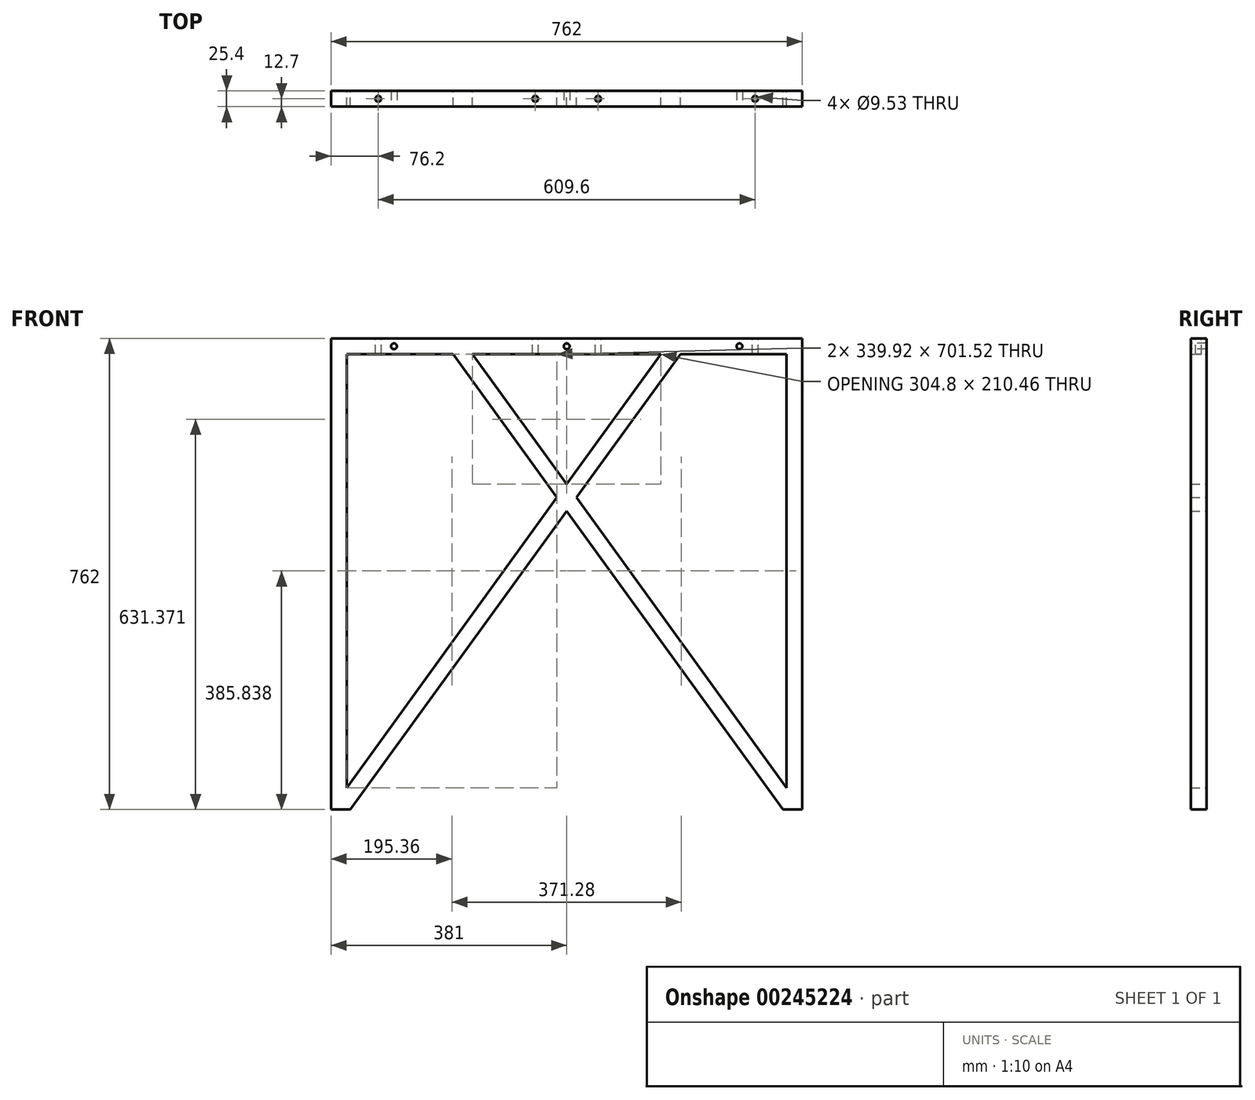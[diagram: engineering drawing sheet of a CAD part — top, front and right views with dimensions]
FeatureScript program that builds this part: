
annotation { "Feature Type Name" : "Feature", "Feature Type Description" : "" }
export const myFeature = defineFeature(function(context is Context, id is Id, definition is map)
    precondition{}
    {
        {
            var Q0;
            Q0=qCreatedBy(makeId("Front.planeOp"),FACE);
            var sketch = newSketch(context, id + "F0", { "sketchPlane" : qUnion([Q0])});
            skLineSegment(sketch, "E0.bottom", {"start": v(-381, 762) * mm, "end": v(381, 762) * mm});
            skLineSegment(sketch, "E0.left", {"start": v(-381, 762) * mm, "end": v(-381, 0) * mm});
            skLineSegment(sketch, "E0.right", {"start": v(381, 762) * mm, "end": v(381, 0) * mm});
            skLineSegment(sketch, "E1", {"start": v(0, 762) * mm, "end": v(0, 0) * mm, "construction": true});
            skLineSegment(sketch, "E2.0", {"start": v(-355.6, 736.6) * mm, "end": v(-355.6, 35.08) * mm});
            skLineSegment(sketch, "E2.2", {"start": v(355.6, 736.6) * mm, "end": v(355.6, 35.08) * mm});
            skLineSegment(sketch, "E3", {"start": v(-355.6, 35.08) * mm, "end": v(-15.68, 504.49) * mm});
            skLineSegment(sketch, "E4.0", {"start": v(-349.64, 0) * mm, "end": v(0, 482.84) * mm});
            skLineSegment(sketch, "E5", {"start": v(-381, 0) * mm, "end": v(-349.64, 0) * mm});
            skLineSegment(sketch, "E6.MirrorCS", {"start": v(349.64, 0) * mm, "end": v(0, 482.84) * mm});
            skLineSegment(sketch, "E7.MirrorCS", {"start": v(355.6, 35.08) * mm, "end": v(15.68, 504.49) * mm});
            skLineSegment(sketch, "E8", {"start": v(381, 0) * mm, "end": v(349.64, 0) * mm});
            skLineSegment(sketch, "E9", {"start": v(-355.6, 736.6) * mm, "end": v(-183.76, 736.6) * mm});
            skLineSegment(sketch, "E10.trimOffspring", {"start": v(-152.4, 736.6) * mm, "end": v(152.4, 736.6) * mm});
            skLineSegment(sketch, "E11.trimOffspring", {"start": v(183.76, 736.6) * mm, "end": v(355.6, 736.6) * mm});
            skLineSegment(sketch, "E12.trimOffspring", {"start": v(15.68, 504.49) * mm, "end": v(183.76, 736.6) * mm});
            skLineSegment(sketch, "E13.trimOffspring", {"start": v(0, 526.14) * mm, "end": v(152.4, 736.6) * mm});
            skLineSegment(sketch, "E14.trimOffspring", {"start": v(0, 526.14) * mm, "end": v(-152.4, 736.6) * mm});
            skLineSegment(sketch, "E15.trimOffspring", {"start": v(-15.68, 504.49) * mm, "end": v(-183.76, 736.6) * mm});
            skSolve(sketch);
        }
        {
            var Q0;
            Q0 = qSketchRegion(id + "F0", true);
            extrude(context, id + "F1", {"entities" : qUnion([Q0]), "depth" : 25.4 * mm});
        }
        {
            var Q0;
            Q0=makeQuery(id+"F1.opExtrude","CAP_FACE",FACE,{"disambiguationData":[OSD([sQuery(id+"F0.wireOp",EDGE,"E0.bottom"),sQuery(id+"F0.wireOp",EDGE,"E0.left"),sQuery(id+"F0.wireOp",EDGE,"E0.right"),sQuery(id+"F0.wireOp",EDGE,"E2.0"),sQuery(id+"F0.wireOp",EDGE,"E2.2"),sQuery(id+"F0.wireOp",EDGE,"E3"),sQuery(id+"F0.wireOp",EDGE,"E4.0"),sQuery(id+"F0.wireOp",EDGE,"E5"),sQuery(id+"F0.wireOp",EDGE,"E6.MirrorCS"),sQuery(id+"F0.wireOp",EDGE,"E7.MirrorCS"),sQuery(id+"F0.wireOp",EDGE,"E8"),sQuery(id+"F0.wireOp",EDGE,"E9"),sQuery(id+"F0.wireOp",EDGE,"E10.trimOffspring"),sQuery(id+"F0.wireOp",EDGE,"E11.trimOffspring"),sQuery(id+"F0.wireOp",EDGE,"E12.trimOffspring"),sQuery(id+"F0.wireOp",EDGE,"E13.trimOffspring"),sQuery(id+"F0.wireOp",EDGE,"E14.trimOffspring"),sQuery(id+"F0.wireOp",EDGE,"E15.trimOffspring")])],"isStart":false});
            var sketch = newSketch(context, id + "F2", { "sketchPlane" : qUnion([Q0])});
            skCircle(sketch, "E16", {"center": v(-279.4, 749.3) * mm, "radius": 4.76 * mm});
            skCircle(sketch, "E17.1.0.0", {"center": v(0, 749.3) * mm, "radius": 4.76 * mm});
            skCircle(sketch, "E17.2.0.0", {"center": v(279.4, 749.3) * mm, "radius": 4.76 * mm});
            skLineSegment(sketch, "E17.direction1", {"start": v(-279.4, 749.3) * mm, "end": v(0, 749.3) * mm, "construction": true});
            skSolve(sketch);
        }
        {
            var Q0;
            Q0 = qSketchRegion(id + "F2", true);
            extrude(context, id + "F3", {"entities" : qUnion([Q0]), "operationType" : NewBodyOperationType.REMOVE, "oppositeDirection" : true, "depth" : 25.4 * mm});
        }
        {
            var Q0;
            Q0=makeQuery(id+"F1.opExtrude","SWEPT_FACE",FACE,{"disambiguationData":[OSD([sQuery(id+"F0.wireOp",EDGE,"E0.bottom")])]});
            var sketch = newSketch(context, id + "F4", { "sketchPlane" : qUnion([Q0])});
            skCircle(sketch, "E18", {"center": v(-50.8, -12.7) * mm, "radius": 4.76 * mm});
            skCircle(sketch, "E19", {"center": v(50.8, -12.7) * mm, "radius": 4.76 * mm});
            skCircle(sketch, "E20", {"center": v(304.8, -12.7) * mm, "radius": 4.76 * mm});
            skCircle(sketch, "E21", {"center": v(-304.8, -12.7) * mm, "radius": 4.76 * mm});
            skSolve(sketch);
        }
        {
            var Q0;
            Q0 = qSketchRegion(id + "F4", true);
            extrude(context, id + "F5", {"entities" : qUnion([Q0]), "operationType" : NewBodyOperationType.REMOVE, "oppositeDirection" : true, "depth" : 25.4 * mm});
        }
    });
